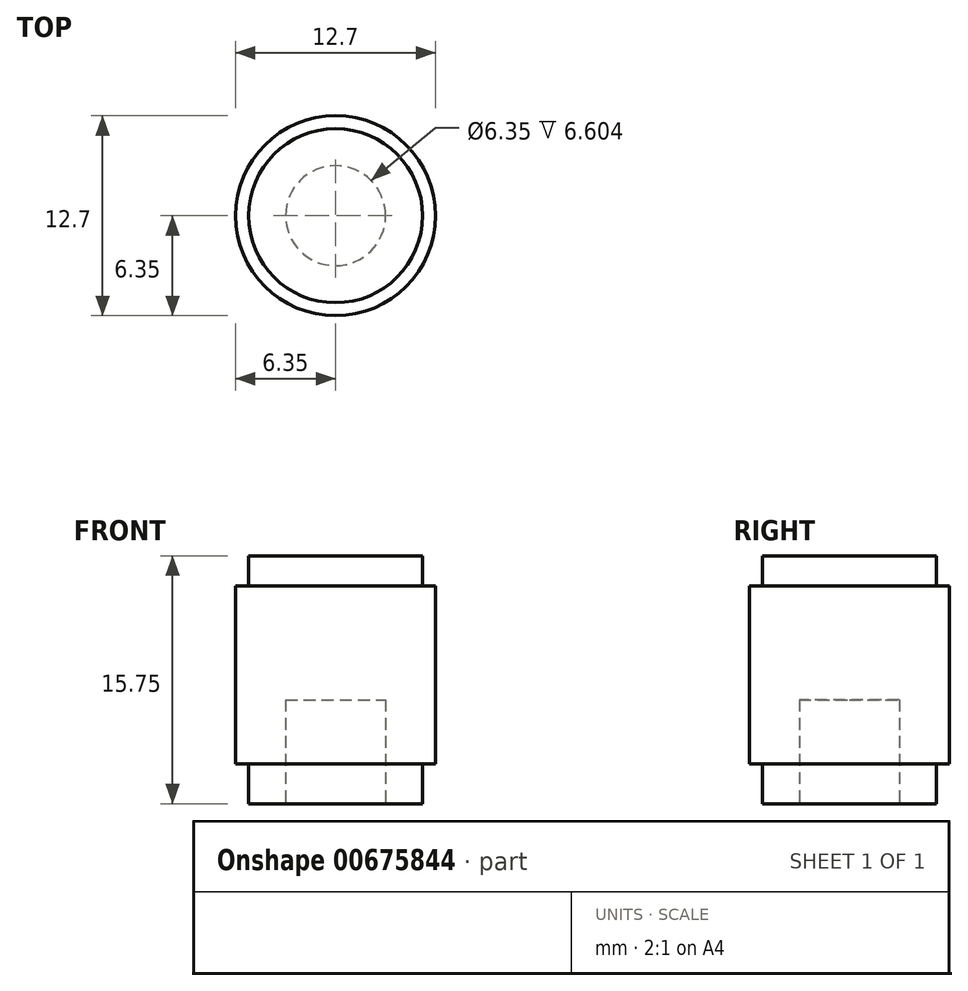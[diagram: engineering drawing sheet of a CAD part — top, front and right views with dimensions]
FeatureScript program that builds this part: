
annotation { "Feature Type Name" : "Feature", "Feature Type Description" : "" }
export const myFeature = defineFeature(function(context is Context, id is Id, definition is map)
    precondition{}
    {
        {
            var Q0;
            Q0=qCreatedBy(makeId("Top.planeOp"),FACE);
            var sketch = newSketch(context, id + "F0", { "sketchPlane" : qUnion([Q0])});
            skCircle(sketch, "E0", {"center": v(0, 0) * mm, "radius": 6.35 * mm});
            skSolve(sketch);
        }
        {
            var Q0;
            Q0 = qSketchRegion(id + "F0", true);
            extrude(context, id + "F1", {"entities" : qUnion([Q0]), "depth" : 11.3 * mm, "offsetDistance" : 25.4 * mm});
        }
        {
            var Q0;
            Q0=makeQuery(id+"F1.opExtrude","CAP_FACE",FACE,{"disambiguationData":[OSD([sQuery(id+"F0.wireOp",EDGE,"E0")])],"isStart":false});
            var sketch = newSketch(context, id + "F2", { "sketchPlane" : qUnion([Q0])});
            skCircle(sketch, "E1", {"center": v(0, 0) * mm, "radius": 5.52 * mm});
            skSolve(sketch);
        }
        {
            var Q0;
            Q0 = qSketchRegion(id + "F2", true);
            extrude(context, id + "F3", {"entities" : qUnion([Q0]), "depth" : 1.9 * mm, "offsetDistance" : 25.4 * mm});
        }
        {
            var Q0;
            Q0=makeQuery(id+"F1.opExtrude","CAP_FACE",FACE,{"disambiguationData":[OSD([sQuery(id+"F0.wireOp",EDGE,"E0")])],"isStart":true});
            var sketch = newSketch(context, id + "F4", { "sketchPlane" : qUnion([Q0])});
            skCircle(sketch, "E2", {"center": v(0, 0) * mm, "radius": 5.52 * mm});
            skSolve(sketch);
        }
        {
            var Q0;
            Q0 = qSketchRegion(id + "F4", true);
            extrude(context, id + "F5", {"entities" : qUnion([Q0]), "operationType" : NewBodyOperationType.ADD, "depth" : 2.54 * mm, "offsetDistance" : 25.4 * mm});
        }
        {
            var Q0;
            Q0=makeQuery(id+"F5.opExtrude","CAP_FACE",FACE,{"disambiguationData":[OSD([sQuery(id+"F4.wireOp",EDGE,"E2")])],"isStart":false});
            var sketch = newSketch(context, id + "F6", { "sketchPlane" : qUnion([Q0])});
            skCircle(sketch, "E3", {"center": v(0, 0) * mm, "radius": 3.18 * mm});
            skSolve(sketch);
        }
        {
            var Q0;
            Q0 = qSketchRegion(id + "F6", true);
            extrude(context, id + "F7", {"entities" : qUnion([Q0]), "operationType" : NewBodyOperationType.REMOVE, "oppositeDirection" : true, "depth" : 6.6 * mm, "offsetDistance" : 25.4 * mm});
        }
    });
